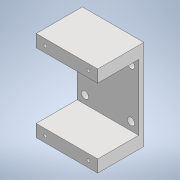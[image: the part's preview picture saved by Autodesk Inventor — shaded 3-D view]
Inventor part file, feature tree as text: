
AUTODESK INVENTOR PART (.ipt)
format: ipt  version: 2022 (Build 260153000, 153)  size: 173,056 bytes
history: native  units: in
note: dims shown in document units (in); Inventor stores cm internally (conversion verified against a paired STEP export)
features: reference x10, extrude x5, sketch x5, other x3, plane x1
ambient origin geometry x8: Origin, YZ Plane, XZ Plane, XY Plane, X Axis, Y Axis, Z Axis, Center Point
bodies: Solid1 (feature_tree)
feature tree (24):
  extrude  "Extrusion1"  Depth=0.4724in
  extrude  "Extrusion2"  Depth=1.5748in TaperAngle=0.0deg
  extrude  "Extrusion3"  Depth=0.1181in
  extrude  "Extrusion4"  Depth=0.1181in
  plane  "Work Plane1"
  extrude  "Extrusion5"  Depth=0.4724in
  sketch  "Sketch1"  dims[d0=0.1969in d1=0.0in d2=0.4724in]
  reference  "Reference1"
  reference  "Reference2"
  reference  "Reference3"
  reference  "Reference4"
  reference  "Reference5"
  reference  "Reference6"
  reference  "Reference7"
  reference  "Reference8"
  reference  "Reference9"
  reference  "Reference10"
  sketch  "Sketch2"  dims[d3=0.4724in d4=1.5748in d5=0.0in]
  sketch  "Sketch3"  dims[d6=0.1181in d7=0.1181in]
  sketch  "Sketch4"  dims[d8=0.1181in d9=0.1181in]
  sketch  "Sketch5"  dims[d10=0.2362in d11=0.2362in d12=1.6535in d13=1.6535in d14=0.3543in d15=0.3543in d16=0.1969in d17=0.0in d18=0.2756in d19=0.2756in d20=0.2756in d21=0.2756in d22=0.1969in d23=0.0in d24=0.9843in d25=0.9843in d26=0.4724in d27=0.0in]
  parser-record x1  (decoder bookkeeping rows leaked as tree rows — omitted from the tree; the rows remain in map.json)
  other  "model.iam"
  other  "base_link:1"
note: 1 file-system path scrubbed to <path> (originals preserved in map.json)
